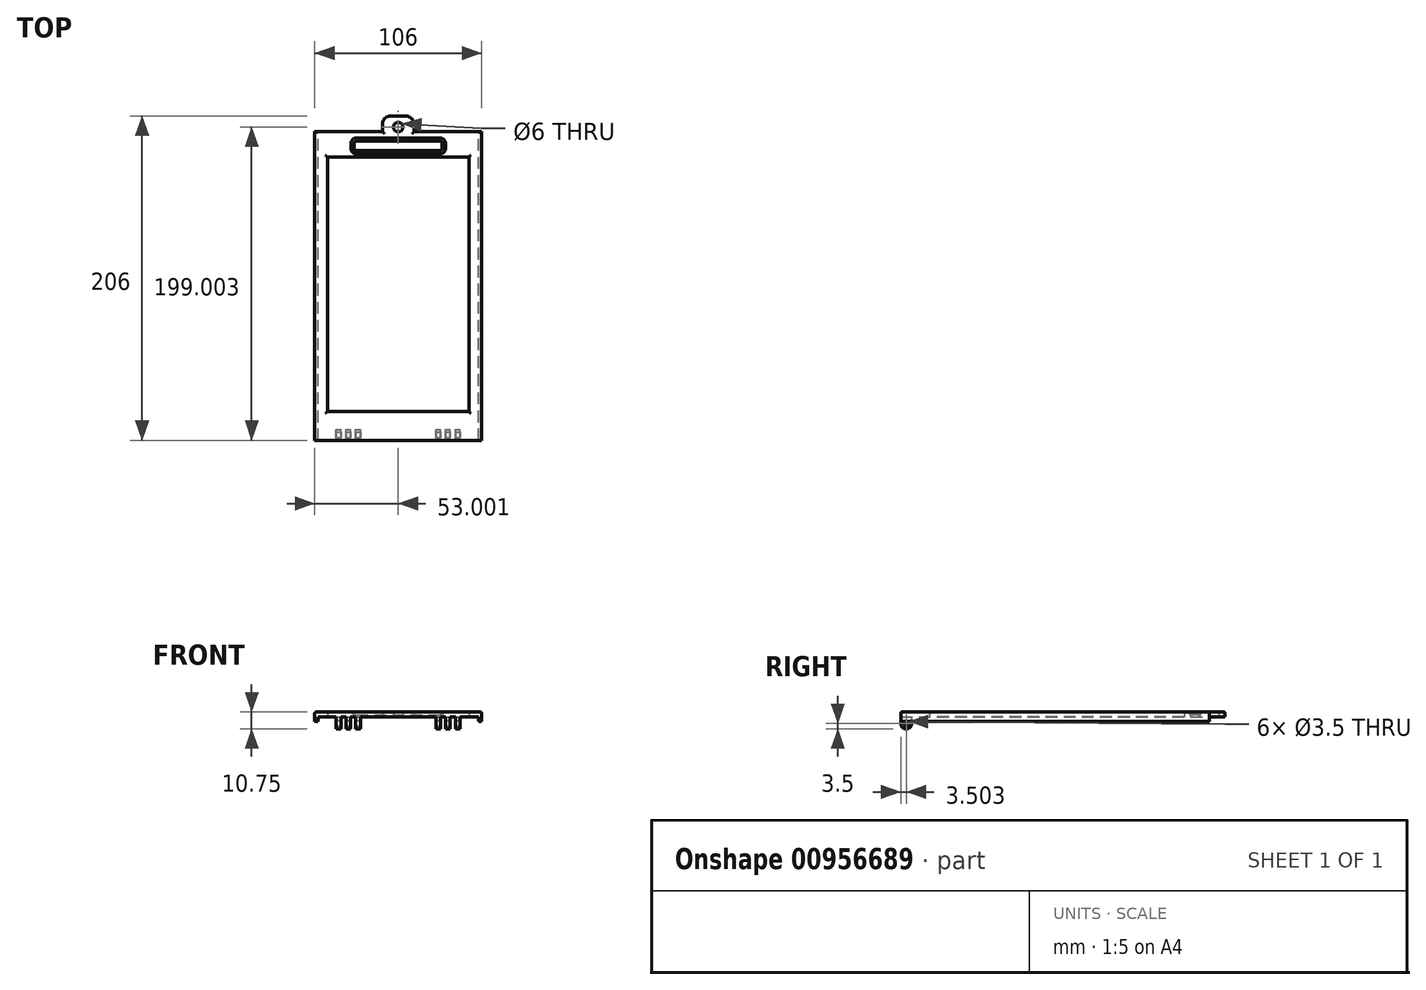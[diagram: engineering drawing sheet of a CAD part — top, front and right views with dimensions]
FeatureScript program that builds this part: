
annotation { "Feature Type Name" : "Feature", "Feature Type Description" : "" }
export const myFeature = defineFeature(function(context is Context, id is Id, definition is map)
    precondition{}
    {
        {
            var Q0;
            Q0=qCreatedBy(makeId("Top.planeOp"),FACE);
            var sketch = newSketch(context, id + "F0", { "sketchPlane" : qUnion([Q0])});
            skLineSegment(sketch, "E0.bottom", {"start": v(-69.72, 12.81) * mm, "end": v(36.28, 12.81) * mm});
            skLineSegment(sketch, "E0.top", {"start": v(-69.72, -175.69) * mm, "end": v(36.28, -175.69) * mm});
            skLineSegment(sketch, "E0.left", {"start": v(-69.72, 12.81) * mm, "end": v(-69.72, -175.69) * mm});
            skLineSegment(sketch, "E0.right", {"start": v(36.28, 12.81) * mm, "end": v(36.28, -175.69) * mm});
            skLineSegment(sketch, "E1.bottom", {"start": v(-61.72, 2.06) * mm, "end": v(28.28, 2.06) * mm, "construction": true});
            skLineSegment(sketch, "E1.top", {"start": v(-61.72, -164.94) * mm, "end": v(28.28, -164.94) * mm});
            skLineSegment(sketch, "E1.left", {"start": v(-61.72, 2.06) * mm, "end": v(-61.72, -164.94) * mm});
            skLineSegment(sketch, "E1.right", {"start": v(28.28, 2.06) * mm, "end": v(28.28, -164.94) * mm});
            skPoint(sketch, "E2", {"position": v(-16.72, 12.81) * mm});
            skPoint(sketch, "E3", {"position": v(-16.72, 2.06) * mm});
            skPoint(sketch, "E4", {"position": v(28.28, -81.44) * mm});
            skPoint(sketch, "E5", {"position": v(36.28, -81.44) * mm});
            skLineSegment(sketch, "E6.top", {"start": v(-69.72, -183.19) * mm, "end": v(36.28, -183.19) * mm});
            skLineSegment(sketch, "E6.left", {"start": v(-69.72, -175.69) * mm, "end": v(-69.72, -183.19) * mm});
            skLineSegment(sketch, "E6.right", {"start": v(36.28, -175.69) * mm, "end": v(36.28, -183.19) * mm});
            skLineSegment(sketch, "E7.0", {"start": v(-61.72, -3.19) * mm, "end": v(28.28, -3.19) * mm});
            skSolve(sketch);
        }
        {
            var Q0;
            Q0 = qSketchRegion(id + "F0", true);
            extrude(context, id + "F1", {"entities" : qUnion([Q0]), "depth" : 3 * mm, "offsetDistance" : 25 * mm});
        }
        {
            var Q0;
            Q0=makeQuery(id+"F1.opExtrude","CAP_FACE",FACE,{"disambiguationData":[OSD([sQuery(id+"F0.wireOp",EDGE,"E0.bottom"),sQuery(id+"F0.wireOp",EDGE,"E0.left"),sQuery(id+"F0.wireOp",EDGE,"E0.right"),sQuery(id+"F0.wireOp",EDGE,"E1.bottom"),sQuery(id+"F0.wireOp",EDGE,"E1.top"),sQuery(id+"F0.wireOp",EDGE,"E1.left"),sQuery(id+"F0.wireOp",EDGE,"E1.right"),sQuery(id+"F0.wireOp",EDGE,"E6.top"),sQuery(id+"F0.wireOp",EDGE,"E6.left"),sQuery(id+"F0.wireOp",EDGE,"E6.right")])],"isStart":true});
            var sketch = newSketch(context, id + "F2", { "sketchPlane" : qUnion([Q0])});
            skLineSegment(sketch, "E8.bottom", {"start": v(-49.82, 183.19) * mm, "end": v(-46.82, 183.19) * mm});
            skLineSegment(sketch, "E8.top", {"start": v(-49.82, 176.19) * mm, "end": v(-46.82, 176.19) * mm});
            skLineSegment(sketch, "E8.left", {"start": v(-49.82, 183.19) * mm, "end": v(-49.82, 176.19) * mm});
            skLineSegment(sketch, "E8.right", {"start": v(-46.82, 183.19) * mm, "end": v(-46.82, 176.19) * mm});
            skLineSegment(sketch, "E9.bottom", {"start": v(13.38, 183.19) * mm, "end": v(16.38, 183.19) * mm});
            skLineSegment(sketch, "E9.top", {"start": v(13.38, 176.19) * mm, "end": v(16.38, 176.19) * mm});
            skLineSegment(sketch, "E9.left", {"start": v(13.38, 183.19) * mm, "end": v(13.38, 176.19) * mm});
            skLineSegment(sketch, "E9.right", {"start": v(16.38, 183.19) * mm, "end": v(16.38, 176.19) * mm});
            skLineSegment(sketch, "E10.bottom", {"start": v(-56.02, 183.19) * mm, "end": v(-53.02, 183.19) * mm});
            skLineSegment(sketch, "E10.top", {"start": v(-56.02, 176.19) * mm, "end": v(-53.02, 176.19) * mm});
            skLineSegment(sketch, "E10.left", {"start": v(-56.02, 183.19) * mm, "end": v(-56.02, 176.19) * mm});
            skLineSegment(sketch, "E10.right", {"start": v(-53.02, 183.19) * mm, "end": v(-53.02, 176.19) * mm});
            skLineSegment(sketch, "E11.bottom", {"start": v(19.58, 183.19) * mm, "end": v(22.58, 183.19) * mm});
            skLineSegment(sketch, "E11.top", {"start": v(19.58, 176.19) * mm, "end": v(22.58, 176.19) * mm});
            skLineSegment(sketch, "E11.left", {"start": v(19.58, 183.19) * mm, "end": v(19.58, 176.19) * mm});
            skLineSegment(sketch, "E11.right", {"start": v(22.58, 183.19) * mm, "end": v(22.58, 176.19) * mm});
            skLineSegment(sketch, "E12.bottom", {"start": v(-43.62, 183.19) * mm, "end": v(-40.62, 183.19) * mm});
            skLineSegment(sketch, "E12.top", {"start": v(-43.62, 176.19) * mm, "end": v(-40.62, 176.19) * mm});
            skLineSegment(sketch, "E12.left", {"start": v(-43.62, 183.19) * mm, "end": v(-43.62, 176.19) * mm});
            skLineSegment(sketch, "E12.right", {"start": v(-40.62, 183.19) * mm, "end": v(-40.62, 176.19) * mm});
            skLineSegment(sketch, "E13.bottom", {"start": v(7.18, 183.19) * mm, "end": v(10.18, 183.19) * mm});
            skLineSegment(sketch, "E13.top", {"start": v(7.18, 176.19) * mm, "end": v(10.18, 176.19) * mm});
            skLineSegment(sketch, "E13.left", {"start": v(7.18, 183.19) * mm, "end": v(7.18, 176.19) * mm});
            skLineSegment(sketch, "E13.right", {"start": v(10.18, 183.19) * mm, "end": v(10.18, 176.19) * mm});
            skSolve(sketch);
        }
        {
            var Q0;
            Q0 = qSketchRegion(id + "F2", true);
            extrude(context, id + "F3", {"entities" : qUnion([Q0]), "operationType" : NewBodyOperationType.ADD, "depth" : 7.75 * mm, "offsetDistance" : 25 * mm});
        }
        {
            var Q0;
            Q0=makeQuery(id+"F3.opExtrude","CAP_EDGE",EDGE,{"disambiguationData":[OSD([sQuery(id+"F2.wireOp",EDGE,"E8.bottom")])],"isStart":false});
            var Q1;
            Q1=makeQuery(id+"F3.opExtrude","CAP_EDGE",EDGE,{"disambiguationData":[OSD([sQuery(id+"F2.wireOp",EDGE,"E8.top")])],"isStart":false});
            var Q2;
            Q2=makeQuery(id+"F3.opExtrude","CAP_EDGE",EDGE,{"disambiguationData":[OSD([sQuery(id+"F2.wireOp",EDGE,"E9.bottom")])],"isStart":false});
            var Q3;
            Q3=makeQuery(id+"F3.opExtrude","CAP_EDGE",EDGE,{"disambiguationData":[OSD([sQuery(id+"F2.wireOp",EDGE,"E9.top")])],"isStart":false});
            var Q4;
            Q4=makeQuery(id+"F3.opExtrude","CAP_EDGE",EDGE,{"disambiguationData":[OSD([sQuery(id+"F2.wireOp",EDGE,"E10.top")])],"isStart":false});
            var Q5;
            Q5=makeQuery(id+"F3.opExtrude","CAP_EDGE",EDGE,{"disambiguationData":[OSD([sQuery(id+"F2.wireOp",EDGE,"E10.bottom")])],"isStart":false});
            var Q6;
            Q6=makeQuery(id+"F3.opExtrude","CAP_EDGE",EDGE,{"disambiguationData":[OSD([sQuery(id+"F2.wireOp",EDGE,"E12.bottom")])],"isStart":false});
            var Q7;
            Q7=makeQuery(id+"F3.opExtrude","CAP_EDGE",EDGE,{"disambiguationData":[OSD([sQuery(id+"F2.wireOp",EDGE,"E12.top")])],"isStart":false});
            var Q8;
            Q8=makeQuery(id+"F3.opExtrude","CAP_EDGE",EDGE,{"disambiguationData":[OSD([sQuery(id+"F2.wireOp",EDGE,"E11.top")])],"isStart":false});
            var Q9;
            Q9=makeQuery(id+"F3.opExtrude","CAP_EDGE",EDGE,{"disambiguationData":[OSD([sQuery(id+"F2.wireOp",EDGE,"E13.top")])],"isStart":false});
            var Q10;
            Q10=makeQuery(id+"F3.opExtrude","CAP_EDGE",EDGE,{"disambiguationData":[OSD([sQuery(id+"F2.wireOp",EDGE,"E13.bottom")])],"isStart":false});
            var Q11;
            Q11=makeQuery(id+"F3.opExtrude","CAP_EDGE",EDGE,{"disambiguationData":[OSD([sQuery(id+"F2.wireOp",EDGE,"E11.bottom")])],"isStart":false});
            fillet(context, id + "F4", {"entities" : qUnion([Q0, Q1, Q2, Q3, Q4, Q5, Q6, Q7, Q8, Q9, Q10, Q11]), "radius" : 3.5 * mm, "tangentPropagation" : true, "allowEdgeOverflow" : false});
        }
        {
            var Q0;
            Q0=makeQuery(id+"F3.opExtrude","SWEPT_FACE",FACE,{"disambiguationData":[OSD([sQuery(id+"F2.wireOp",EDGE,"E9.right")])]});
            var sketch = newSketch(context, id + "F5", { "sketchPlane" : qUnion([Q0])});
            skCircle(sketch, "E14", {"center": v(-179.69, -4.25) * mm, "radius": 1.75 * mm});
            skSolve(sketch);
        }
        {
            var Q0;
            Q0 = qSketchRegion(id + "F5", true);
            extrude(context, id + "F6", {"entities" : qUnion([Q0]), "operationType" : NewBodyOperationType.REMOVE, "endBound" : BoundingType.THROUGH_ALL, "oppositeDirection" : true, "depth" : 25 * mm, "offsetDistance" : 25 * mm});
        }
        {
            var Q0;
            Q0=makeQuery(id+"F1.opExtrude","SWEPT_FACE",FACE,{"disambiguationData":[OSD([sQuery(id+"F0.wireOp",EDGE,"E0.bottom")])]});
            var sketch = newSketch(context, id + "F7", { "sketchPlane" : qUnion([Q0])});
            skLineSegment(sketch, "E15.bottom", {"start": v(26.72, 3) * mm, "end": v(6.72, 3) * mm});
            skLineSegment(sketch, "E15.top", {"start": v(26.72, 0) * mm, "end": v(6.72, 0) * mm});
            skLineSegment(sketch, "E15.left", {"start": v(26.72, 3) * mm, "end": v(26.72, 0) * mm});
            skLineSegment(sketch, "E15.right", {"start": v(6.72, 3) * mm, "end": v(6.72, 0) * mm});
            skPoint(sketch, "E16", {"position": v(16.72, 3) * mm});
            skPoint(sketch, "E17", {"position": v(16.72, 0) * mm});
            skSolve(sketch);
        }
        {
            var Q0;
            Q0 = qSketchRegion(id + "F7", true);
            extrude(context, id + "F8", {"entities" : qUnion([Q0]), "operationType" : NewBodyOperationType.ADD, "depth" : 10 * mm, "offsetDistance" : 25 * mm});
        }
        {
            var Q0;
            Q0=makeQuery(id+"F8.boolean.opBoolean","MERGE",FACE,{"derivedFrom":[makeQuery(id+"F1.opExtrude","CAP_FACE",FACE,{"disambiguationData":[OSD([sQuery(id+"F0.wireOp",EDGE,"E0.bottom"),sQuery(id+"F0.wireOp",EDGE,"E0.left"),sQuery(id+"F0.wireOp",EDGE,"E0.right"),sQuery(id+"F0.wireOp",EDGE,"E1.bottom"),sQuery(id+"F0.wireOp",EDGE,"E1.top"),sQuery(id+"F0.wireOp",EDGE,"E1.left"),sQuery(id+"F0.wireOp",EDGE,"E1.right"),sQuery(id+"F0.wireOp",EDGE,"E6.top"),sQuery(id+"F0.wireOp",EDGE,"E6.left"),sQuery(id+"F0.wireOp",EDGE,"E6.right")])],"isStart":true}),makeQuery(id+"F8.opExtrude","SWEPT_FACE",FACE,{"disambiguationData":[OSD([sQuery(id+"F7.wireOp",EDGE,"E15.top")])]})]});
            var sketch = newSketch(context, id + "F9", { "sketchPlane" : qUnion([Q0])});
            skPoint(sketch, "E18", {"position": v(-16.72, -15.65) * mm});
            skPoint(sketch, "E19.0", {"position": v(-16.72, -22.81) * mm});
            skPoint(sketch, "E20", {"position": v(-16.72, -16.33) * mm});
            skCircle(sketch, "E21", {"center": v(-16.72, -15.81) * mm, "radius": 3 * mm});
            skSolve(sketch);
        }
        {
            var Q0;
            Q0 = qSketchRegion(id + "F9", true);
            extrude(context, id + "F10", {"entities" : qUnion([Q0]), "operationType" : NewBodyOperationType.REMOVE, "endBound" : BoundingType.THROUGH_ALL, "oppositeDirection" : true, "depth" : 25 * mm, "offsetDistance" : 25 * mm});
        }
        {
            var Q0;
            Q0=makeQuery(id+"F8.boolean.opBoolean","MERGE",FACE,{"derivedFrom":[makeQuery(id+"F1.opExtrude","CAP_FACE",FACE,{"disambiguationData":[OSD([sQuery(id+"F0.wireOp",EDGE,"E0.bottom"),sQuery(id+"F0.wireOp",EDGE,"E0.left"),sQuery(id+"F0.wireOp",EDGE,"E0.right"),sQuery(id+"F0.wireOp",EDGE,"E1.bottom"),sQuery(id+"F0.wireOp",EDGE,"E1.top"),sQuery(id+"F0.wireOp",EDGE,"E1.left"),sQuery(id+"F0.wireOp",EDGE,"E1.right"),sQuery(id+"F0.wireOp",EDGE,"E6.top"),sQuery(id+"F0.wireOp",EDGE,"E6.left"),sQuery(id+"F0.wireOp",EDGE,"E6.right")])],"isStart":true}),makeQuery(id+"F8.opExtrude","SWEPT_FACE",FACE,{"disambiguationData":[OSD([sQuery(id+"F7.wireOp",EDGE,"E15.top")])]})]});
            var sketch = newSketch(context, id + "F11", { "sketchPlane" : qUnion([Q0])});
            skLineSegment(sketch, "E22.bottom", {"start": v(36.28, 183.19) * mm, "end": v(34.28, 183.19) * mm});
            skLineSegment(sketch, "E22.top", {"start": v(36.28, -12.81) * mm, "end": v(34.28, -12.81) * mm});
            skLineSegment(sketch, "E22.left", {"start": v(36.28, 183.19) * mm, "end": v(36.28, -12.81) * mm});
            skLineSegment(sketch, "E22.right", {"start": v(34.28, 183.19) * mm, "end": v(34.28, -12.81) * mm});
            skLineSegment(sketch, "E23.bottom", {"start": v(-69.72, 183.19) * mm, "end": v(-67.72, 183.19) * mm});
            skLineSegment(sketch, "E23.top", {"start": v(-69.72, -12.81) * mm, "end": v(-67.72, -12.81) * mm});
            skLineSegment(sketch, "E23.left", {"start": v(-69.72, 183.19) * mm, "end": v(-69.72, -12.81) * mm});
            skLineSegment(sketch, "E23.right", {"start": v(-67.72, 183.19) * mm, "end": v(-67.72, -12.81) * mm});
            skSolve(sketch);
        }
        {
            var Q0;
            Q0=makeQuery(id+"F11.imprint","IMPRINT",FACE,{"disambiguationData":[TD([[makeQuery(id+"F11.imprint","IMPRINT",EDGE,{"derivedFrom":sQuery(id+"F11.wireOp",EDGE,"E22.bottom")}),-1.0]])]});
            var Q1;
            Q1=makeQuery(id+"F11.imprint","IMPRINT",FACE,{"disambiguationData":[TD([[makeQuery(id+"F11.imprint","IMPRINT",EDGE,{"derivedFrom":sQuery(id+"F11.wireOp",EDGE,"E23.bottom")}),-1.0]])]});
            extrude(context, id + "F12", {"entities" : qUnion([Q0, Q1]), "operationType" : NewBodyOperationType.ADD, "depth" : 3 * mm, "offsetDistance" : 25 * mm});
        }
        {
            var Q0;
            Q0=makeQuery(id+"F8.boolean.opBoolean","MERGE",FACE,{"derivedFrom":[makeQuery(id+"F1.opExtrude","CAP_FACE",FACE,{"disambiguationData":[OSD([sQuery(id+"F0.wireOp",EDGE,"E0.bottom"),sQuery(id+"F0.wireOp",EDGE,"E0.left"),sQuery(id+"F0.wireOp",EDGE,"E0.right"),sQuery(id+"F0.wireOp",EDGE,"E1.bottom"),sQuery(id+"F0.wireOp",EDGE,"E1.top"),sQuery(id+"F0.wireOp",EDGE,"E1.left"),sQuery(id+"F0.wireOp",EDGE,"E1.right"),sQuery(id+"F0.wireOp",EDGE,"E6.top"),sQuery(id+"F0.wireOp",EDGE,"E6.left"),sQuery(id+"F0.wireOp",EDGE,"E6.right")])],"isStart":false}),makeQuery(id+"F8.opExtrude","SWEPT_FACE",FACE,{"disambiguationData":[OSD([sQuery(id+"F7.wireOp",EDGE,"E15.bottom")])]})]});
            fillet(context, id + "F13", {"entities" : qUnion([Q0]), "radius" : 1 * mm, "tangentPropagation" : true, "allowEdgeOverflow" : false});
        }
        {
            var Q0;
            Q0=makeQuery(id+"F3.opExtrude","SWEPT_FACE",FACE,{"disambiguationData":[OSD([sQuery(id+"F2.wireOp",EDGE,"E11.right")])]});
            var sketch = newSketch(context, id + "F14", { "sketchPlane" : qUnion([Q0])});
            skCircle(sketch, "E24.0", {"center": v(-179.69, -4.25) * mm, "radius": 1.75 * mm});
            skSolve(sketch);
        }
        {
            var Q0;
            Q0=makeQuery(id+"F14.imprint","IMPRINT",FACE,{"disambiguationData":[TD([[makeQuery(id+"F14.imprint","IMPRINT",EDGE,{"derivedFrom":sQuery(id+"F14.wireOp",EDGE,"E24.0")}),1.0]])]});
            extrude(context, id + "F15", {"entities" : qUnion([Q0]), "operationType" : NewBodyOperationType.REMOVE, "oppositeDirection" : true, "depth" : 25 * mm, "offsetDistance" : 25 * mm});
        }
        {
            var Q0;
            Q0=makeQuery(id+"F8.opExtrude","CAP_EDGE",EDGE,{"disambiguationData":[OSD([sQuery(id+"F7.wireOp",EDGE,"E15.right")])],"isStart":false});
            var Q1;
            Q1=makeQuery(id+"F8.opExtrude","CAP_EDGE",EDGE,{"disambiguationData":[OSD([sQuery(id+"F7.wireOp",EDGE,"E15.left")])],"isStart":false});
            fillet(context, id + "F16", {"entities" : qUnion([Q0, Q1]), "radius" : 5 * mm, "tangentPropagation" : true, "allowEdgeOverflow" : false});
        }
        {
            var Q0;
            Q0=makeQuery(id+"F8.boolean.opBoolean","MERGE",FACE,{"derivedFrom":[makeQuery(id+"F1.opExtrude","CAP_FACE",FACE,{"disambiguationData":[OSD([sQuery(id+"F0.wireOp",EDGE,"E0.bottom"),sQuery(id+"F0.wireOp",EDGE,"E0.left"),sQuery(id+"F0.wireOp",EDGE,"E0.right"),sQuery(id+"F0.wireOp",EDGE,"E1.top"),sQuery(id+"F0.wireOp",EDGE,"E1.left"),sQuery(id+"F0.wireOp",EDGE,"E1.right"),sQuery(id+"F0.wireOp",EDGE,"E6.top"),sQuery(id+"F0.wireOp",EDGE,"E6.left"),sQuery(id+"F0.wireOp",EDGE,"E6.right"),sQuery(id+"F0.wireOp",EDGE,"E7.0")])],"isStart":true}),makeQuery(id+"F8.opExtrude","SWEPT_FACE",FACE,{"disambiguationData":[OSD([sQuery(id+"F7.wireOp",EDGE,"E15.top")])]})]});
            var sketch = newSketch(context, id + "F17", { "sketchPlane" : qUnion([Q0])});
            skLineSegment(sketch, "E25.bottom", {"start": v(-43.33, -0.81) * mm, "end": v(9.9, -0.81) * mm});
            skLineSegment(sketch, "E25.top", {"start": v(-43.33, -6.81) * mm, "end": v(9.9, -6.81) * mm});
            skLineSegment(sketch, "E25.left", {"start": v(-44.72, -2.2) * mm, "end": v(-44.72, -5.42) * mm});
            skLineSegment(sketch, "E25.right", {"start": v(11.28, -2.2) * mm, "end": v(11.28, -5.42) * mm});
            skPoint(sketch, "E26.visualSharp", {"position": v(11.28, -0.81) * mm});
            skArc(sketch, "E26.filletArc", {"start": v(11.28, -2.2) * mm, "mid": v(10.87, -1.22) * mm, "end": v(9.9, -0.81) * mm});
            skPoint(sketch, "E27.visualSharp", {"position": v(-44.72, -0.81) * mm});
            skArc(sketch, "E27.filletArc", {"start": v(-43.33, -0.81) * mm, "mid": v(-44.31, -1.22) * mm, "end": v(-44.72, -2.2) * mm});
            skPoint(sketch, "E28.visualSharp", {"position": v(-44.72, -6.81) * mm});
            skArc(sketch, "E28.filletArc", {"start": v(-44.72, -5.42) * mm, "mid": v(-44.31, -6.4) * mm, "end": v(-43.33, -6.81) * mm});
            skPoint(sketch, "E29.visualSharp", {"position": v(11.28, -6.81) * mm});
            skArc(sketch, "E29.filletArc", {"start": v(9.9, -6.81) * mm, "mid": v(10.87, -6.4) * mm, "end": v(11.28, -5.42) * mm});
            skSolve(sketch);
        }
        {
            var Q0;
            Q0=makeQuery(id+"F17.imprint","IMPRINT",FACE,{"disambiguationData":[TD([[makeQuery(id+"F17.imprint","IMPRINT",EDGE,{"derivedFrom":sQuery(id+"F17.wireOp",EDGE,"E25.bottom")}),-1.0]])]});
            extrude(context, id + "F18", {"entities" : qUnion([Q0]), "operationType" : NewBodyOperationType.REMOVE, "endBound" : BoundingType.THROUGH_ALL, "oppositeDirection" : true, "depth" : 25 * mm, "offsetDistance" : 25 * mm});
        }
        {
            var Q0;
            Q0=makeQuery(id+"F18.boolean.opBoolean","INTERSECT",EDGE,{"derivedFrom":[makeQuery(id+"F8.boolean.opBoolean","MERGE",FACE,{"derivedFrom":[makeQuery(id+"F1.opExtrude","CAP_FACE",FACE,{"disambiguationData":[OSD([sQuery(id+"F0.wireOp",EDGE,"E0.bottom"),sQuery(id+"F0.wireOp",EDGE,"E0.left"),sQuery(id+"F0.wireOp",EDGE,"E0.right"),sQuery(id+"F0.wireOp",EDGE,"E1.top"),sQuery(id+"F0.wireOp",EDGE,"E1.left"),sQuery(id+"F0.wireOp",EDGE,"E1.right"),sQuery(id+"F0.wireOp",EDGE,"E6.top"),sQuery(id+"F0.wireOp",EDGE,"E6.left"),sQuery(id+"F0.wireOp",EDGE,"E6.right"),sQuery(id+"F0.wireOp",EDGE,"E7.0")])],"isStart":false}),makeQuery(id+"F8.opExtrude","SWEPT_FACE",FACE,{"disambiguationData":[OSD([sQuery(id+"F7.wireOp",EDGE,"E15.bottom")])]})]}),makeQuery(id+"F18.opExtrude","SWEPT_FACE",FACE,{"disambiguationData":[OSD([sQuery(id+"F17.wireOp",EDGE,"E25.top")])]})]});
            chamfer(context, id + "F19", {"entities" : qUnion([Q0]), "width" : 2 * mm, "tangentPropagation" : true});
        }
    });
